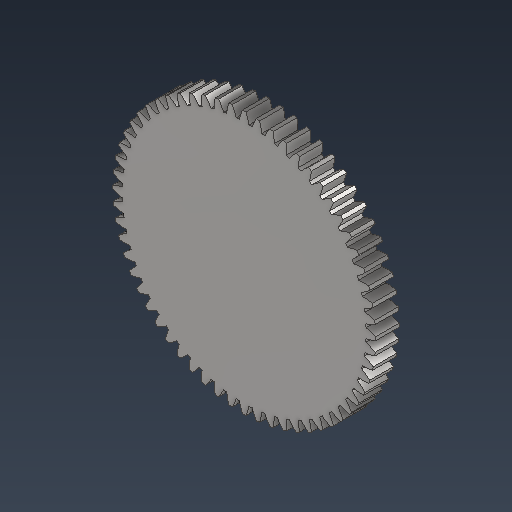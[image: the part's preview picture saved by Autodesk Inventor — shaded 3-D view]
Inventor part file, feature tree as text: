
AUTODESK INVENTOR PART (.ipt)
format: ipt  version: 2021 (Build 250183000, 183)  size: 384,000 bytes
history: native  units: mm (DEFAULTED — no unit token found)
features: plane x3, other x3, sketch x2, extrude x1
ambient origin geometry x8: Origin, YZ Plane, XZ Plane, XY Plane, X Axis, Y Axis, Z Axis, Center Point
bodies: Solid1 (feature_tree)
feature tree (9):
  extrude  "Extrusion1"  Depth=0.5mm TaperAngle=0.0deg
  plane  "Work Plane2"
  plane  "Work Plane8"
  plane  "Work Plane9"
  other  "Engrenagem reta"
  sketch  "Sketch1"  dims[d0=5.575441mm d1=0.5mm d2=0.0mm]
  sketch  "Sketch2"  dims[d3=5.4mm d4=10.0mm d5=0.0mm d16=3.597721mm d17=0.0mm d34=0.523599mm d39=0.0mm d41=0.0mm d43=3.597721mm d46=3.597721mm d47=0.0mm d48=0.0mm]
  other  "Srf1"
  other  "Diâmetro do flanco"
